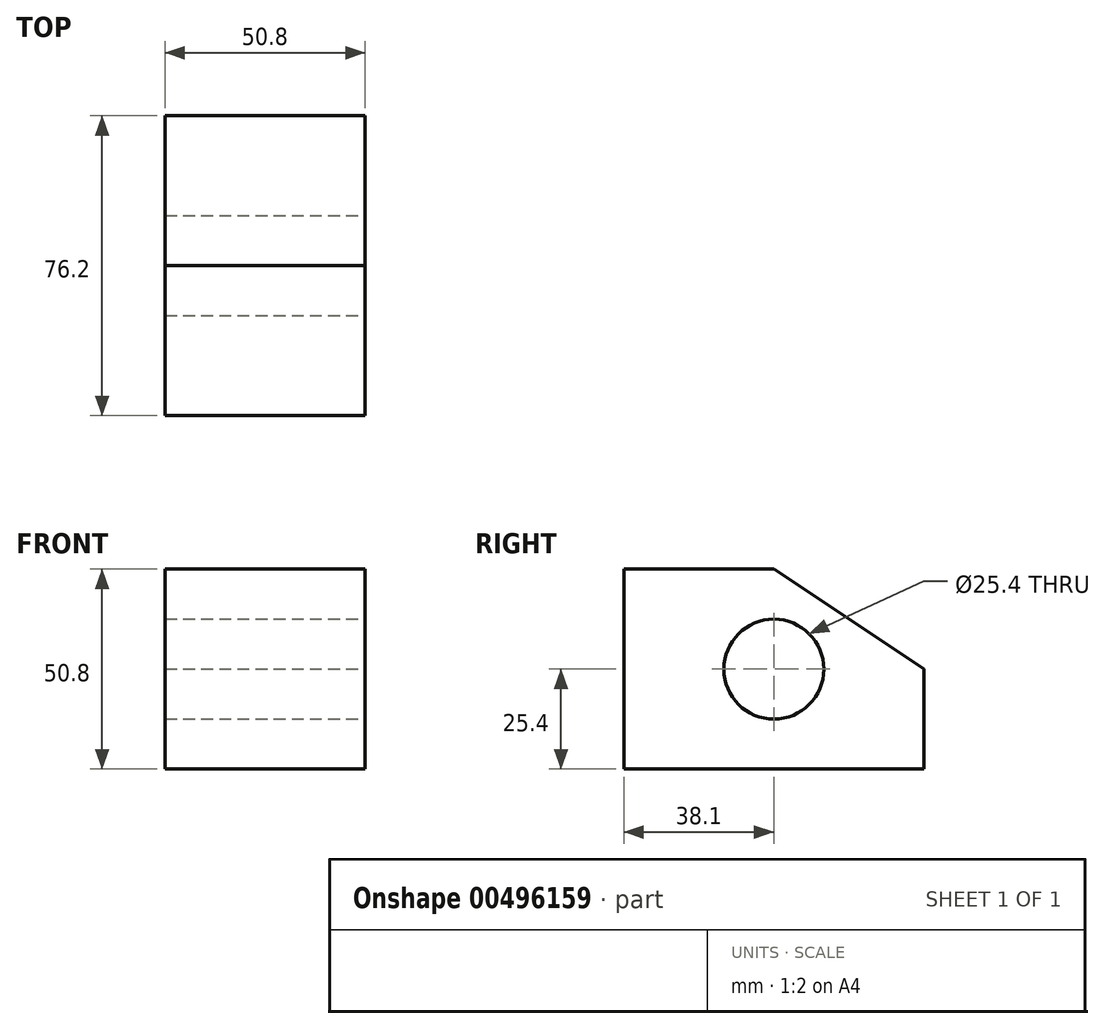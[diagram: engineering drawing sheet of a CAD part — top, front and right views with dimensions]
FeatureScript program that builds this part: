
annotation { "Feature Type Name" : "Feature", "Feature Type Description" : "" }
export const myFeature = defineFeature(function(context is Context, id is Id, definition is map)
    precondition{}
    {
        {
            var Q0;
            Q0=qCreatedBy(makeId("Top.planeOp"),FACE);
            var sketch = newSketch(context, id + "F0", { "sketchPlane" : qUnion([Q0])});
            skLineSegment(sketch, "E0.bottom", {"start": v(0, 0) * mm, "end": v(50.8, 0) * mm});
            skLineSegment(sketch, "E0.top", {"start": v(0, 76.2) * mm, "end": v(50.8, 76.2) * mm});
            skLineSegment(sketch, "E0.left", {"start": v(0, 0) * mm, "end": v(0, 76.2) * mm});
            skLineSegment(sketch, "E0.right", {"start": v(50.8, 0) * mm, "end": v(50.8, 76.2) * mm});
            skSolve(sketch);
        }
        {
            var Q0;
            Q0 = qSketchRegion(id + "F0", true);
            extrude(context, id + "F1", {"entities" : qUnion([Q0]), "depth" : 50.8 * mm});
        }
        {
            var Q0;
            Q0=makeQuery(id+"F1.opExtrude","SWEPT_FACE",FACE,{"disambiguationData":[OSD([sQuery(id+"F0.wireOp",EDGE,"E0.right")])]});
            var sketch = newSketch(context, id + "F2", { "sketchPlane" : qUnion([Q0])});
            skCircle(sketch, "E1", {"center": v(38.1, 25.4) * mm, "radius": 12.7 * mm});
            skSolve(sketch);
        }
        {
            var Q0;
            Q0 = qSketchRegion(id + "F2", true);
            var Q1;
            Q1=makeQuery(id+"F2.imprint","IMPRINT",FACE,{"disambiguationData":[TD([[makeQuery(id+"F2.imprint","IMPRINT",EDGE,{"derivedFrom":sQuery(id+"F2.wireOp",EDGE,"E1")}),1.0]])]});
            extrude(context, id + "F3", {"entities" : qUnion([Q0, Q1]), "operationType" : NewBodyOperationType.REMOVE, "endBound" : BoundingType.UP_TO_NEXT, "oppositeDirection" : true, "depth" : 25.4 * mm});
        }
        {
            var Q0;
            Q0=makeQuery(id+"F1.opExtrude","SWEPT_FACE",FACE,{"disambiguationData":[OSD([sQuery(id+"F0.wireOp",EDGE,"E0.right")])]});
            var sketch = newSketch(context, id + "F4", { "sketchPlane" : qUnion([Q0])});
            skLineSegment(sketch, "E2", {"start": v(38.1, 50.8) * mm, "end": v(76.2, 25.4) * mm});
            skSolve(sketch);
        }
        {
            var Q0;
            {var subQ0=sQuery(id+"F4.wireOp",EDGE,"E2");Q0=makeQuery(id+"F4.imprint","IMPRINT",FACE,{"disambiguationData":[TD([[makeQuery(id+"F4.imprint","IMPRINT",EDGE,{"derivedFrom":subQ0}),1.0]])]});}
            extrude(context, id + "F5", {"entities" : qUnion([Q0]), "operationType" : NewBodyOperationType.REMOVE, "endBound" : BoundingType.UP_TO_NEXT, "oppositeDirection" : true, "depth" : 25.4 * mm});
        }
    });
